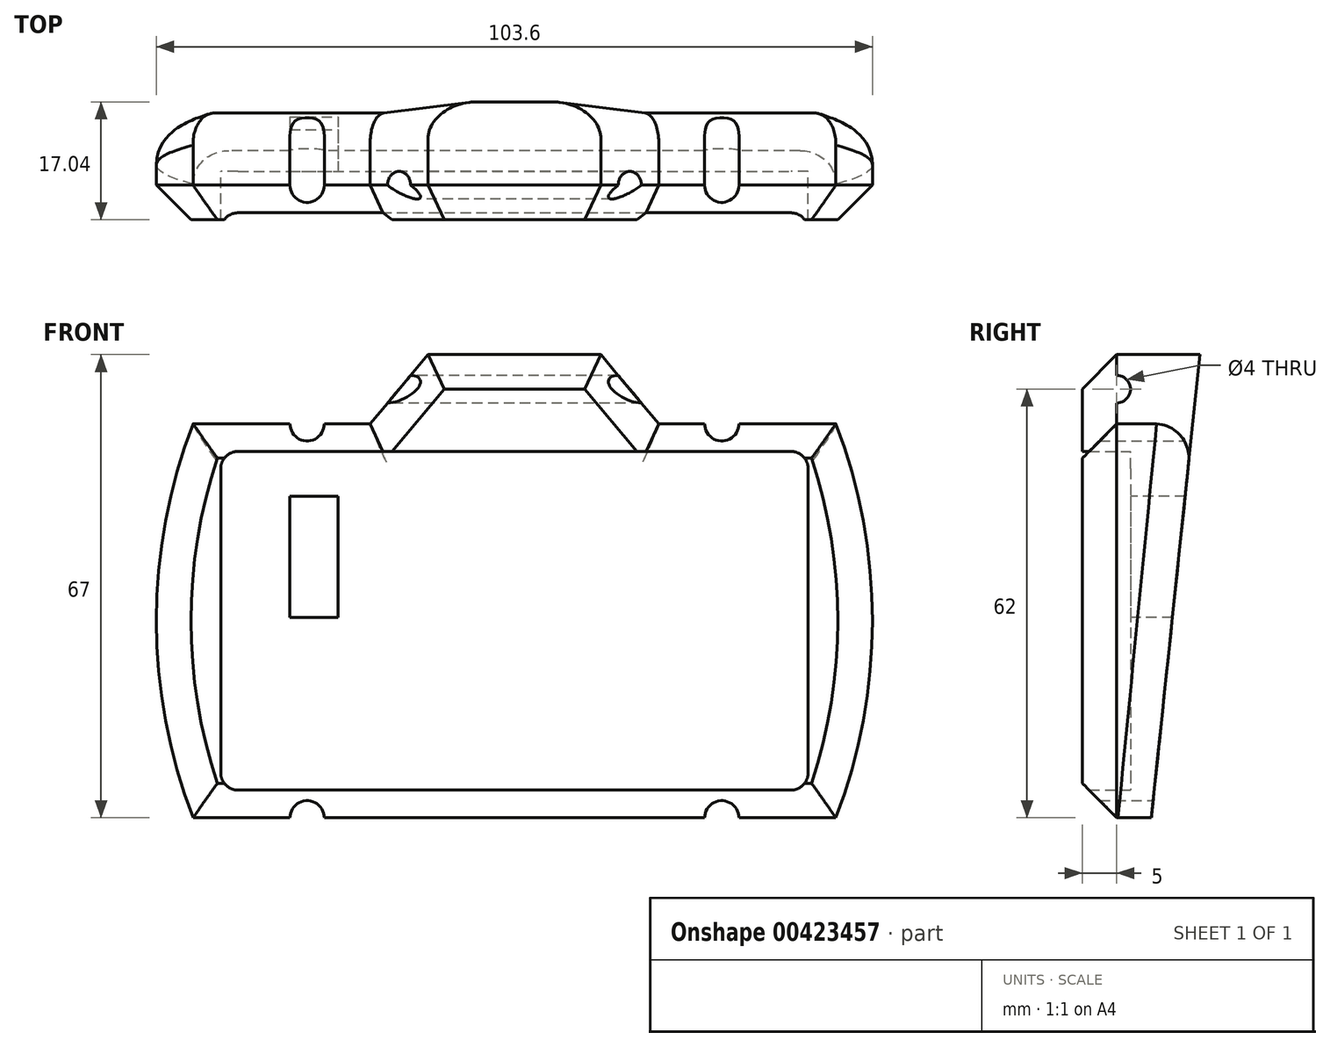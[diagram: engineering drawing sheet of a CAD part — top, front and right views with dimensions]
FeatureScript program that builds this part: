
annotation { "Feature Type Name" : "Feature", "Feature Type Description" : "" }
export const myFeature = defineFeature(function(context is Context, id is Id, definition is map)
    precondition{}
    {
        {
            var Q0;
            Q0=qCreatedBy(makeId("Front.planeOp"),FACE);
            var sketch = newSketch(context, id + "F0", { "sketchPlane" : qUnion([Q0])});
            skLineSegment(sketch, "E0.bottom", {"start": v(86.5, 4) * mm, "end": v(6.5, 4) * mm});
            skLineSegment(sketch, "E0.top", {"start": v(86.5, 53) * mm, "end": v(6.5, 53) * mm});
            skLineSegment(sketch, "E0.left", {"start": v(89, 6.5) * mm, "end": v(89, 50.5) * mm});
            skLineSegment(sketch, "E0.right", {"start": v(4, 6.5) * mm, "end": v(4, 50.5) * mm});
            skPoint(sketch, "E1.visualSharp", {"position": v(89, 4) * mm});
            skArc(sketch, "E1.filletArc", {"start": v(86.5, 4) * mm, "mid": v(88.27, 4.73) * mm, "end": v(89, 6.5) * mm});
            skPoint(sketch, "E2.visualSharp", {"position": v(89, 53) * mm});
            skArc(sketch, "E2.filletArc", {"start": v(89, 50.5) * mm, "mid": v(88.27, 52.27) * mm, "end": v(86.5, 53) * mm});
            skPoint(sketch, "E3.visualSharp", {"position": v(4, 53) * mm});
            skArc(sketch, "E3.filletArc", {"start": v(6.5, 53) * mm, "mid": v(4.73, 52.27) * mm, "end": v(4, 50.5) * mm});
            skPoint(sketch, "E4.visualSharp", {"position": v(4, 4) * mm});
            skArc(sketch, "E4.filletArc", {"start": v(4, 6.5) * mm, "mid": v(4.73, 4.73) * mm, "end": v(6.5, 4) * mm});
            skLineSegment(sketch, "E5.bottom", {"start": v(0, 57) * mm, "end": v(93, 57) * mm});
            skLineSegment(sketch, "E5.top", {"start": v(0, 0) * mm, "end": v(93, 0) * mm});
            skLineSegment(sketch, "E5.left", {"start": v(0, 57) * mm, "end": v(0, 0) * mm});
            skLineSegment(sketch, "E5.right", {"start": v(93, 57) * mm, "end": v(93, 0) * mm});
            skArc(sketch, "E6", {"start": v(0, 57) * mm, "mid": v(-5.3, 28.5) * mm, "end": v(0, 0) * mm});
            skArc(sketch, "E7", {"start": v(93, 0) * mm, "mid": v(98.3, 28.5) * mm, "end": v(93, 57) * mm});
            skPoint(sketch, "E8", {"position": v(-5.3, 28.5) * mm});
            skLineSegment(sketch, "E9", {"start": v(34, 67) * mm, "end": v(59, 67) * mm});
            skLineSegment(sketch, "E10", {"start": v(34, 67) * mm, "end": v(25.6, 57) * mm});
            skLineSegment(sketch, "E11", {"start": v(59, 67) * mm, "end": v(67.4, 57) * mm});
            skLineSegment(sketch, "E12", {"start": v(34, 67) * mm, "end": v(34, 57) * mm});
            skLineSegment(sketch, "E13", {"start": v(59, 67) * mm, "end": v(59, 57) * mm});
            skSolve(sketch);
        }
        {
            var Q0;
            Q0=makeQuery(id+"F0.imprint","IMPRINT",FACE,{"disambiguationData":[TD([[makeQuery(id+"F0.imprint","IMPRINT",EDGE,{"derivedFrom":sQuery(id+"F0.wireOp",EDGE,"E0.bottom")}),-1.0]])]});
            var Q1;
            Q1=makeQuery(id+"F0.imprint","IMPRINT",FACE,{"disambiguationData":[TD([[makeQuery(id+"F0.imprint","IMPRINT",EDGE,{"derivedFrom":sQuery(id+"F0.wireOp",EDGE,"E0.bottom")}),1.0]])]});
            var Q2;
            Q2=makeQuery(id+"F0.imprint","IMPRINT",FACE,{"disambiguationData":[TD([[makeQuery(id+"F0.imprint","IMPRINT",EDGE,{"derivedFrom":sQuery(id+"F0.wireOp",EDGE,"E5.left")}),-1.0]])]});
            var Q3;
            Q3=makeQuery(id+"F0.imprint","IMPRINT",FACE,{"disambiguationData":[TD([[makeQuery(id+"F0.imprint","IMPRINT",EDGE,{"derivedFrom":sQuery(id+"F0.wireOp",EDGE,"E5.right")}),1.0]])]});
            var Q4;
            {var subQ0=sQuery(id+"F0.wireOp",EDGE,"3fx2YpcI-U5EB-vFxf-iBCI-2TCYV5EJUoEd");Q4=makeQuery(id+"F0.imprint","IMPRINT",FACE,{"disambiguationData":[TD([[makeQuery(id+"F0.imprint","IMPRINT",EDGE,{"derivedFrom":subQ0}),-1.0]])]});}
            var Q5;
            {var subQ0=sQuery(id+"F0.wireOp",EDGE,"nPDYfrPs-5EqB-b0Kh-mRlZ-kWoabQpu5ybp");Q5=makeQuery(id+"F0.imprint","IMPRINT",FACE,{"disambiguationData":[TD([[makeQuery(id+"F0.imprint","IMPRINT",EDGE,{"derivedFrom":subQ0}),-1.0]])]});}
            var Q6;
            {var subQ0=sQuery(id+"F0.wireOp",EDGE,"nPDYfrPs-5EqB-b0Kh-mRlZ-kWoabQpu5ybp");Q6=makeQuery(id+"F0.imprint","IMPRINT",FACE,{"disambiguationData":[TD([[makeQuery(id+"F0.imprint","IMPRINT",EDGE,{"derivedFrom":subQ0}),1.0]])]});}
            var Q7;
            Q7=makeQuery(id+"F0.imprint","IMPRINT",FACE,{"disambiguationData":[TD([[makeQuery(id+"F0.imprint","IMPRINT",EDGE,{"derivedFrom":sQuery(id+"F0.wireOp",EDGE,"E9")}),-1.0]])]});
            var Q8;
            {var subQ0=sQuery(id+"F0.wireOp",EDGE,"E10");Q8=makeQuery(id+"F0.imprint","IMPRINT",FACE,{"disambiguationData":[TD([[makeQuery(id+"F0.imprint","IMPRINT",EDGE,{"derivedFrom":subQ0}),1.0]])]});}
            var Q9;
            {var subQ0=sQuery(id+"F0.wireOp",EDGE,"E11");Q9=makeQuery(id+"F0.imprint","IMPRINT",FACE,{"disambiguationData":[TD([[makeQuery(id+"F0.imprint","IMPRINT",EDGE,{"derivedFrom":subQ0}),-1.0]])]});}
            extrude(context, id + "F1", {"entities" : qUnion([Q0, Q1, Q2, Q3, Q4, Q5, Q6, Q7, Q8, Q9]), "depth" : 3 * mm, "offsetDistance" : 25 * mm});
        }
        {
            var Q0;
            Q0=makeQuery(id+"F0.imprint","IMPRINT",FACE,{"disambiguationData":[TD([[makeQuery(id+"F0.imprint","IMPRINT",EDGE,{"derivedFrom":sQuery(id+"F0.wireOp",EDGE,"E9")}),-1.0]])]});
            var Q1;
            {var subQ0=sQuery(id+"F0.wireOp",EDGE,"E10");Q1=makeQuery(id+"F0.imprint","IMPRINT",FACE,{"disambiguationData":[TD([[makeQuery(id+"F0.imprint","IMPRINT",EDGE,{"derivedFrom":subQ0}),1.0]])]});}
            var Q2;
            {var subQ0=sQuery(id+"F0.wireOp",EDGE,"E11");Q2=makeQuery(id+"F0.imprint","IMPRINT",FACE,{"disambiguationData":[TD([[makeQuery(id+"F0.imprint","IMPRINT",EDGE,{"derivedFrom":subQ0}),-1.0]])]});}
            var Q3;
            Q3=makeQuery(id+"F0.imprint","IMPRINT",FACE,{"disambiguationData":[TD([[makeQuery(id+"F0.imprint","IMPRINT",EDGE,{"derivedFrom":sQuery(id+"F0.wireOp",EDGE,"E0.bottom")}),1.0]])]});
            var Q4;
            Q4=makeQuery(id+"F0.imprint","IMPRINT",FACE,{"disambiguationData":[TD([[makeQuery(id+"F0.imprint","IMPRINT",EDGE,{"derivedFrom":sQuery(id+"F0.wireOp",EDGE,"E5.right")}),1.0]])]});
            var Q5;
            Q5=makeQuery(id+"F0.imprint","IMPRINT",FACE,{"disambiguationData":[TD([[makeQuery(id+"F0.imprint","IMPRINT",EDGE,{"derivedFrom":sQuery(id+"F0.wireOp",EDGE,"E5.left")}),-1.0]])]});
            extrude(context, id + "F2", {"entities" : qUnion([Q0, Q1, Q2, Q3, Q4, Q5]), "operationType" : NewBodyOperationType.ADD, "depth" : 10 * mm, "offsetDistance" : 25 * mm});
        }
        {
            var Q0;
            Q0=qCreatedBy(makeId("Right.planeOp"),FACE);
            var sketch = newSketch(context, id + "F3", { "sketchPlane" : qUnion([Q0])});
            skLineSegment(sketch, "E14.0", {"start": v(0, 0) * mm, "end": v(0, 57) * mm});
            skLineSegment(sketch, "E14.1", {"start": v(0, 67) * mm, "end": v(0, 57) * mm});
            skLineSegment(sketch, "E14.2", {"start": v(10, 67) * mm, "end": v(0, 67) * mm});
            skLineSegment(sketch, "E14.3", {"start": v(10, 67) * mm, "end": v(10, 57) * mm});
            skLineSegment(sketch, "E14.4", {"start": v(10, 0) * mm, "end": v(10, 57) * mm});
            skLineSegment(sketch, "E14.5", {"start": v(10, 0) * mm, "end": v(0, 0) * mm});
            skLineSegment(sketch, "E15", {"start": v(0, 0) * mm, "end": v(7.04, 67) * mm});
            skSolve(sketch);
        }
        {
            var Q0;
            Q0=makeQuery(id+"F1.opExtrude","CAP_FACE",FACE,{"disambiguationData":[OSD([sQuery(id+"F0.wireOp",EDGE,"E5.bottom"),sQuery(id+"F0.wireOp",EDGE,"E5.top"),sQuery(id+"F0.wireOp",EDGE,"E6"),sQuery(id+"F0.wireOp",EDGE,"E7"),sQuery(id+"F0.wireOp",EDGE,"E9"),sQuery(id+"F0.wireOp",EDGE,"E10"),sQuery(id+"F0.wireOp",EDGE,"E11")])],"isStart":true});
            extrude(context, id + "F4", {"entities" : qUnion([Q0]), "operationType" : NewBodyOperationType.ADD, "depth" : 10 * mm, "offsetDistance" : 25 * mm});
        }
        {
            var Q0;
            {var subQ0=sQuery(id+"F3.wireOp",EDGE,"E14.3");Q0=makeQuery(id+"F3.imprint","IMPRINT",FACE,{"disambiguationData":[TD([[makeQuery(id+"F3.imprint","IMPRINT",EDGE,{"derivedFrom":subQ0}),-1.0]])]});}
            extrude(context, id + "F5", {"entities" : qUnion([Q0]), "operationType" : NewBodyOperationType.REMOVE, "endBound" : BoundingType.SYMMETRIC, "depth" : 300 * mm, "offsetDistance" : 25 * mm});
        }
        {
            var Q0;
            Q0=makeQuery(id+"F2.opExtrude","SWEPT_FACE",FACE,{"disambiguationData":[OSD([sQuery(id+"F0.wireOp",EDGE,"E0.right")])]});
            var sketch = newSketch(context, id + "F6", { "sketchPlane" : qUnion([Q0])});
            skLineSegment(sketch, "E16.0.0", {"start": v(0, 67) * mm, "end": v(0, 57) * mm});
            skLineSegment(sketch, "E16.0.1", {"start": v(0, 57) * mm, "end": v(-10, 57) * mm});
            skLineSegment(sketch, "E16.0.2", {"start": v(-10, 57) * mm, "end": v(-10, 67) * mm});
            skLineSegment(sketch, "E16.0.3", {"start": v(-10, 67) * mm, "end": v(0, 67) * mm});
            skCircle(sketch, "E17", {"center": v(-5, 62) * mm, "radius": 2 * mm});
            skSolve(sketch);
        }
        {
            var Q0;
            Q0=makeQuery(id+"F6.imprint","IMPRINT",FACE,{"disambiguationData":[TD([[makeQuery(id+"F6.imprint","IMPRINT",EDGE,{"derivedFrom":sQuery(id+"F6.wireOp",EDGE,"E17")}),1.0]])]});
            extrude(context, id + "F7", {"entities" : qUnion([Q0]), "operationType" : NewBodyOperationType.REMOVE, "endBound" : BoundingType.THROUGH_ALL, "depth" : 25 * mm, "offsetDistance" : 25 * mm});
        }
        {
            var Q0;
            Q0=makeQuery(id+"F2.opExtrude","CAP_EDGE",EDGE,{"disambiguationData":[OSD([sQuery(id+"F0.wireOp",EDGE,"E6")])],"isStart":false});
            var Q1;
            {var subQ0=sQuery(id+"F0.wireOp",EDGE,"E5.bottom");Q1=makeQuery(id+"F2.opExtrude","CAP_EDGE",EDGE,{"disambiguationData":[OSD([subQ0]),TDD([makeQuery(id+"F0.imprint","IMPRINT",EDGE,{"disambiguationData":[TD([[makeQuery(id+"F0.imprint","INTERSECT",VERTEX,{"derivedFrom":[subQ0,sQuery(id+"F0.wireOp",EDGE,"E10")]}),1.0]])],"derivedFrom":subQ0})])],"isStart":false});}
            var Q2;
            Q2=makeQuery(id+"F2.opExtrude","CAP_EDGE",EDGE,{"disambiguationData":[OSD([sQuery(id+"F0.wireOp",EDGE,"E10")])],"isStart":false});
            var Q3;
            Q3=makeQuery(id+"F2.opExtrude","CAP_EDGE",EDGE,{"disambiguationData":[OSD([sQuery(id+"F0.wireOp",EDGE,"E9")])],"isStart":false});
            var Q4;
            Q4=makeQuery(id+"F2.opExtrude","CAP_EDGE",EDGE,{"disambiguationData":[OSD([sQuery(id+"F0.wireOp",EDGE,"E11")])],"isStart":false});
            var Q5;
            {var subQ0=sQuery(id+"F0.wireOp",EDGE,"E5.bottom");Q5=makeQuery(id+"F2.opExtrude","CAP_EDGE",EDGE,{"disambiguationData":[OSD([subQ0]),TDD([makeQuery(id+"F0.imprint","IMPRINT",EDGE,{"disambiguationData":[TD([[makeQuery(id+"F0.imprint","INTERSECT",VERTEX,{"derivedFrom":[subQ0,sQuery(id+"F0.wireOp",EDGE,"E11")]}),-1.0]])],"derivedFrom":subQ0})])],"isStart":false});}
            var Q6;
            Q6=makeQuery(id+"F2.opExtrude","CAP_EDGE",EDGE,{"disambiguationData":[OSD([sQuery(id+"F0.wireOp",EDGE,"E5.top")])],"isStart":false});
            var Q7;
            Q7=makeQuery(id+"F2.opExtrude","CAP_EDGE",EDGE,{"disambiguationData":[OSD([sQuery(id+"F0.wireOp",EDGE,"E7")])],"isStart":false});
            chamfer(context, id + "F8", {"entities" : qUnion([Q0, Q1, Q2, Q3, Q4, Q5, Q6, Q7]), "width" : 5 * mm, "tangentPropagation" : true});
        }
        {
            var Q0;
            Q0=makeQuery(id+"F1.opExtrude","CAP_FACE",FACE,{"disambiguationData":[OSD([sQuery(id+"F0.wireOp",EDGE,"E5.bottom"),sQuery(id+"F0.wireOp",EDGE,"E5.top"),sQuery(id+"F0.wireOp",EDGE,"E6"),sQuery(id+"F0.wireOp",EDGE,"E7"),sQuery(id+"F0.wireOp",EDGE,"E9"),sQuery(id+"F0.wireOp",EDGE,"E10"),sQuery(id+"F0.wireOp",EDGE,"E11")])],"isStart":false});
            var sketch = newSketch(context, id + "F9", { "sketchPlane" : qUnion([Q0])});
            skLineSegment(sketch, "E18.0", {"start": v(4, 6.5) * mm, "end": v(4, 50.5) * mm});
            skLineSegment(sketch, "E18.1", {"start": v(89, 6.5) * mm, "end": v(89, 50.5) * mm});
            skArc(sketch, "E19", {"start": v(14, 57) * mm, "mid": v(16.5, 54.5) * mm, "end": v(19, 57) * mm});
            skArc(sketch, "E20", {"start": v(19, 0) * mm, "mid": v(16.5, 2.5) * mm, "end": v(14, 0) * mm});
            skArc(sketch, "E21", {"start": v(74, 57) * mm, "mid": v(76.5, 54.5) * mm, "end": v(79, 57) * mm});
            skArc(sketch, "E22", {"start": v(79, 0) * mm, "mid": v(76.5, 2.5) * mm, "end": v(74, 0) * mm});
            skLineSegment(sketch, "E23", {"start": v(14, 57) * mm, "end": v(19, 57) * mm});
            skLineSegment(sketch, "E24", {"start": v(74, 57) * mm, "end": v(79, 57) * mm});
            skLineSegment(sketch, "E25", {"start": v(74, 0) * mm, "end": v(79, 0) * mm});
            skLineSegment(sketch, "E26", {"start": v(14, 0) * mm, "end": v(19, 0) * mm});
            skSolve(sketch);
        }
        {
            var Q0;
            {var subQ0=sQuery(id+"F9.wireOp",EDGE,"E19");Q0=makeQuery(id+"F9.imprint","IMPRINT",FACE,{"disambiguationData":[TD([[makeQuery(id+"F9.imprint","IMPRINT",EDGE,{"derivedFrom":subQ0}),1.0]])]});}
            var Q1;
            {var subQ0=sQuery(id+"F9.wireOp",EDGE,"E21");Q1=makeQuery(id+"F9.imprint","IMPRINT",FACE,{"disambiguationData":[TD([[makeQuery(id+"F9.imprint","IMPRINT",EDGE,{"derivedFrom":subQ0}),1.0]])]});}
            var Q2;
            {var subQ0=sQuery(id+"F9.wireOp",EDGE,"E22");Q2=makeQuery(id+"F9.imprint","IMPRINT",FACE,{"disambiguationData":[TD([[makeQuery(id+"F9.imprint","IMPRINT",EDGE,{"derivedFrom":subQ0}),1.0]])]});}
            var Q3;
            {var subQ0=sQuery(id+"F9.wireOp",EDGE,"E20");Q3=makeQuery(id+"F9.imprint","IMPRINT",FACE,{"disambiguationData":[TD([[makeQuery(id+"F9.imprint","IMPRINT",EDGE,{"derivedFrom":subQ0}),1.0]])]});}
            var Q4;
            Q4=sQuery(id+"F9.wireOp",EDGE,"E22");
            var Q5;
            Q5=sQuery(id+"F9.wireOp",EDGE,"E20");
            var Q6;
            Q6=sQuery(id+"F9.wireOp",EDGE,"E19");
            var Q7;
            Q7=sQuery(id+"F9.wireOp",EDGE,"E21");
            extrude(context, id + "F10", {"entities" : qUnion([Q0, Q1, Q2, Q3]), "operationType" : NewBodyOperationType.REMOVE, "surfaceEntities" : qUnion([Q4, Q5, Q6, Q7]), "endBound" : BoundingType.SYMMETRIC, "depth" : 25 * mm, "offsetDistance" : 25 * mm});
        }
        {
            var Q0;
            {var subQ0=sQuery(id+"F0.wireOp",EDGE,"E7");Q0=makeQuery(id+"F5.boolean.opBoolean","INTERSECT",EDGE,{"derivedFrom":[makeQuery(id+"F4.boolean.opBoolean","MERGE",FACE,{"derivedFrom":[makeQuery(id+"F2.boolean.opBoolean","MERGE",FACE,{"derivedFrom":[makeQuery(id+"F1.opExtrude","SWEPT_FACE",FACE,{"disambiguationData":[OSD([subQ0])]}),makeQuery(id+"F2.opExtrude","SWEPT_FACE",FACE,{"disambiguationData":[OSD([subQ0])]})]}),makeQuery(id+"F4.opExtrude","SWEPT_FACE",FACE,{"disambiguationData":[OSD([subQ0])]})]}),makeQuery(id+"F5.opExtrude","SWEPT_FACE",FACE,{"disambiguationData":[OSD([sQuery(id+"F3.wireOp",EDGE,"E15")])]})]});}
            var Q1;
            {var subQ0=sQuery(id+"F0.wireOp",EDGE,"E5.bottom");var subQ1=makeQuery(id+"F0.imprint","IMPRINT",EDGE,{"disambiguationData":[TD([[makeQuery(id+"F0.imprint","INTERSECT",VERTEX,{"derivedFrom":[subQ0,sQuery(id+"F0.wireOp",EDGE,"E11")]}),-1.0]])],"derivedFrom":subQ0});Q1=makeQuery(id+"F5.boolean.opBoolean","INTERSECT",EDGE,{"derivedFrom":[makeQuery(id+"F4.boolean.opBoolean","MERGE",FACE,{"derivedFrom":[makeQuery(id+"F2.boolean.opBoolean","MERGE",FACE,{"derivedFrom":[makeQuery(id+"F1.opExtrude","SWEPT_FACE",FACE,{"disambiguationData":[OSD([subQ0]),TDD([subQ1])]}),makeQuery(id+"F2.opExtrude","SWEPT_FACE",FACE,{"disambiguationData":[OSD([subQ0]),TDD([subQ1])]})]}),makeQuery(id+"F4.opExtrude","SWEPT_FACE",FACE,{"disambiguationData":[OSD([subQ0]),TDD([makeQuery(id+"F1.opExtrude","CAP_EDGE",EDGE,{"disambiguationData":[OSD([subQ0]),TDD([subQ1])],"isStart":true})])]})]}),makeQuery(id+"F5.opExtrude","SWEPT_FACE",FACE,{"disambiguationData":[OSD([sQuery(id+"F3.wireOp",EDGE,"E15")])]})]});}
            var Q2;
            {var subQ0=sQuery(id+"F0.wireOp",EDGE,"E11");Q2=makeQuery(id+"F5.boolean.opBoolean","INTERSECT",EDGE,{"derivedFrom":[makeQuery(id+"F4.boolean.opBoolean","MERGE",FACE,{"derivedFrom":[makeQuery(id+"F2.boolean.opBoolean","MERGE",FACE,{"derivedFrom":[makeQuery(id+"F1.opExtrude","SWEPT_FACE",FACE,{"disambiguationData":[OSD([subQ0])]}),makeQuery(id+"F2.opExtrude","SWEPT_FACE",FACE,{"disambiguationData":[OSD([subQ0])]})]}),makeQuery(id+"F4.opExtrude","SWEPT_FACE",FACE,{"disambiguationData":[OSD([subQ0])]})]}),makeQuery(id+"F5.opExtrude","SWEPT_FACE",FACE,{"disambiguationData":[OSD([sQuery(id+"F3.wireOp",EDGE,"E15")])]})]});}
            var Q3;
            Q3=makeQuery(id+"F5.boolean.opBoolean","COPY",EDGE,{"derivedFrom":makeQuery(id+"F5.opExtrude","SWEPT_EDGE",EDGE,{"disambiguationData":[OSD([sQuery(id+"F3.wireOp",EDGE,"E14.2"),sQuery(id+"F3.wireOp",EDGE,"E15")])]})});
            var Q4;
            {var subQ0=sQuery(id+"F0.wireOp",EDGE,"E10");Q4=makeQuery(id+"F5.boolean.opBoolean","INTERSECT",EDGE,{"derivedFrom":[makeQuery(id+"F4.boolean.opBoolean","MERGE",FACE,{"derivedFrom":[makeQuery(id+"F2.boolean.opBoolean","MERGE",FACE,{"derivedFrom":[makeQuery(id+"F1.opExtrude","SWEPT_FACE",FACE,{"disambiguationData":[OSD([subQ0])]}),makeQuery(id+"F2.opExtrude","SWEPT_FACE",FACE,{"disambiguationData":[OSD([subQ0])]})]}),makeQuery(id+"F4.opExtrude","SWEPT_FACE",FACE,{"disambiguationData":[OSD([subQ0])]})]}),makeQuery(id+"F5.opExtrude","SWEPT_FACE",FACE,{"disambiguationData":[OSD([sQuery(id+"F3.wireOp",EDGE,"E15")])]})]});}
            var Q5;
            {var subQ0=sQuery(id+"F0.wireOp",EDGE,"E10");var subQ1=sQuery(id+"F0.wireOp",EDGE,"E5.bottom");var subQ2=makeQuery(id+"F0.imprint","IMPRINT",EDGE,{"disambiguationData":[TD([[makeQuery(id+"F0.imprint","INTERSECT",VERTEX,{"derivedFrom":[subQ1,subQ0]}),1.0]])],"derivedFrom":subQ1});var subQ3=makeQuery(id+"F4.opExtrude","SWEPT_FACE",FACE,{"disambiguationData":[OSD([subQ1]),TDD([makeQuery(id+"F1.opExtrude","CAP_EDGE",EDGE,{"disambiguationData":[OSD([subQ1]),TDD([subQ2])],"isStart":true})])]});var subQ4=makeQuery(id+"F2.opExtrude","SWEPT_FACE",FACE,{"disambiguationData":[OSD([subQ1]),TDD([subQ2])]});var subQ5=makeQuery(id+"F1.opExtrude","SWEPT_FACE",FACE,{"disambiguationData":[OSD([subQ1]),TDD([subQ2])]});var subQ6=makeQuery(id+"F5.opExtrude","SWEPT_FACE",FACE,{"disambiguationData":[OSD([sQuery(id+"F3.wireOp",EDGE,"E15")])]});Q5=makeQuery(id+"F10.boolean.opBoolean","SPLIT",EDGE,{"disambiguationData":[TD([makeQuery(id+"F1.opExtrude","SWEPT_FACE",FACE,{"disambiguationData":[OSD([subQ0])]})])],"derivedFrom":makeQuery(id+"F5.boolean.opBoolean","INTERSECT",EDGE,{"derivedFrom":[makeQuery(id+"F4.boolean.opBoolean","MERGE",FACE,{"derivedFrom":[makeQuery(id+"F2.boolean.opBoolean","MERGE",FACE,{"derivedFrom":[subQ5,subQ4]}),subQ3]}),subQ6]})});}
            var Q6;
            {var subQ0=sQuery(id+"F0.wireOp",EDGE,"E6");var subQ1=sQuery(id+"F0.wireOp",EDGE,"E5.bottom");var subQ2=makeQuery(id+"F0.imprint","IMPRINT",EDGE,{"disambiguationData":[TD([[makeQuery(id+"F0.imprint","INTERSECT",VERTEX,{"derivedFrom":[subQ1,sQuery(id+"F0.wireOp",EDGE,"E10")]}),1.0]])],"derivedFrom":subQ1});var subQ3=makeQuery(id+"F2.opExtrude","SWEPT_FACE",FACE,{"disambiguationData":[OSD([subQ1]),TDD([subQ2])]});var subQ4=makeQuery(id+"F1.opExtrude","SWEPT_FACE",FACE,{"disambiguationData":[OSD([subQ1]),TDD([subQ2])]});var subQ5=makeQuery(id+"F4.opExtrude","SWEPT_FACE",FACE,{"disambiguationData":[OSD([subQ1]),TDD([makeQuery(id+"F1.opExtrude","CAP_EDGE",EDGE,{"disambiguationData":[OSD([subQ1]),TDD([subQ2])],"isStart":true})])]});var subQ6=makeQuery(id+"F5.opExtrude","SWEPT_FACE",FACE,{"disambiguationData":[OSD([sQuery(id+"F3.wireOp",EDGE,"E15")])]});Q6=makeQuery(id+"F10.boolean.opBoolean","SPLIT",EDGE,{"disambiguationData":[TD([makeQuery(id+"F1.opExtrude","SWEPT_FACE",FACE,{"disambiguationData":[OSD([subQ0])]})])],"derivedFrom":makeQuery(id+"F5.boolean.opBoolean","INTERSECT",EDGE,{"derivedFrom":[makeQuery(id+"F4.boolean.opBoolean","MERGE",FACE,{"derivedFrom":[makeQuery(id+"F2.boolean.opBoolean","MERGE",FACE,{"derivedFrom":[subQ4,subQ3]}),subQ5]}),subQ6]})});}
            var Q7;
            {var subQ0=sQuery(id+"F0.wireOp",EDGE,"E6");Q7=makeQuery(id+"F5.boolean.opBoolean","INTERSECT",EDGE,{"derivedFrom":[makeQuery(id+"F4.boolean.opBoolean","MERGE",FACE,{"derivedFrom":[makeQuery(id+"F2.boolean.opBoolean","MERGE",FACE,{"derivedFrom":[makeQuery(id+"F1.opExtrude","SWEPT_FACE",FACE,{"disambiguationData":[OSD([subQ0])]}),makeQuery(id+"F2.opExtrude","SWEPT_FACE",FACE,{"disambiguationData":[OSD([subQ0])]})]}),makeQuery(id+"F4.opExtrude","SWEPT_FACE",FACE,{"disambiguationData":[OSD([subQ0])]})]}),makeQuery(id+"F5.opExtrude","SWEPT_FACE",FACE,{"disambiguationData":[OSD([sQuery(id+"F3.wireOp",EDGE,"E15")])]})]});}
            var Q8;
            {var subQ0=sQuery(id+"F0.wireOp",EDGE,"E5.top");var subQ1=sQuery(id+"F0.wireOp",EDGE,"E6");var subQ2=sQuery(id+"F3.wireOp",EDGE,"E15");Q8=makeQuery(id+"F10.boolean.opBoolean","SPLIT",EDGE,{"disambiguationData":[TD([makeQuery(id+"F1.opExtrude","SWEPT_FACE",FACE,{"disambiguationData":[OSD([subQ0])]}),makeQuery(id+"F1.opExtrude","SWEPT_FACE",FACE,{"disambiguationData":[OSD([subQ1])]}),makeQuery(id+"F2.opExtrude","SWEPT_FACE",FACE,{"disambiguationData":[OSD([subQ0])]}),makeQuery(id+"F2.opExtrude","SWEPT_FACE",FACE,{"disambiguationData":[OSD([subQ1])]}),makeQuery(id+"F4.opExtrude","SWEPT_FACE",FACE,{"disambiguationData":[OSD([subQ0])]}),makeQuery(id+"F4.opExtrude","SWEPT_FACE",FACE,{"disambiguationData":[OSD([subQ1])]}),makeQuery(id+"F5.boolean.opBoolean","COPY",FACE,{"derivedFrom":makeQuery(id+"F5.opExtrude","SWEPT_FACE",FACE,{"disambiguationData":[OSD([subQ2])]})}),makeQuery(id+"F10.opExtrude","SWEPT_FACE",FACE,{"disambiguationData":[OSD([sQuery(id+"F9.wireOp",EDGE,"E20")])]})])],"derivedFrom":makeQuery(id+"F5.boolean.opBoolean","COPY",EDGE,{"derivedFrom":makeQuery(id+"F5.opExtrude","SWEPT_EDGE",EDGE,{"disambiguationData":[OSD([sQuery(id+"F3.wireOp",EDGE,"E14.0"),sQuery(id+"F3.wireOp",EDGE,"E14.5"),subQ2])]})})});}
            var Q9;
            {var subQ0=sQuery(id+"F0.wireOp",EDGE,"E5.top");var subQ1=sQuery(id+"F3.wireOp",EDGE,"E15");Q9=makeQuery(id+"F10.boolean.opBoolean","SPLIT",EDGE,{"disambiguationData":[TD([makeQuery(id+"F1.opExtrude","SWEPT_FACE",FACE,{"disambiguationData":[OSD([subQ0])]}),makeQuery(id+"F2.opExtrude","SWEPT_FACE",FACE,{"disambiguationData":[OSD([subQ0])]}),makeQuery(id+"F4.opExtrude","SWEPT_FACE",FACE,{"disambiguationData":[OSD([subQ0])]}),makeQuery(id+"F5.boolean.opBoolean","COPY",FACE,{"derivedFrom":makeQuery(id+"F5.opExtrude","SWEPT_FACE",FACE,{"disambiguationData":[OSD([subQ1])]})}),makeQuery(id+"F10.opExtrude","SWEPT_FACE",FACE,{"disambiguationData":[OSD([sQuery(id+"F9.wireOp",EDGE,"E20")])]}),makeQuery(id+"F10.opExtrude","SWEPT_FACE",FACE,{"disambiguationData":[OSD([sQuery(id+"F9.wireOp",EDGE,"E22")])]})])],"derivedFrom":makeQuery(id+"F5.boolean.opBoolean","COPY",EDGE,{"derivedFrom":makeQuery(id+"F5.opExtrude","SWEPT_EDGE",EDGE,{"disambiguationData":[OSD([sQuery(id+"F3.wireOp",EDGE,"E14.0"),sQuery(id+"F3.wireOp",EDGE,"E14.5"),subQ1])]})})});}
            var Q10;
            {var subQ0=sQuery(id+"F0.wireOp",EDGE,"E7");var subQ1=sQuery(id+"F0.wireOp",EDGE,"E5.top");var subQ2=sQuery(id+"F3.wireOp",EDGE,"E15");Q10=makeQuery(id+"F10.boolean.opBoolean","SPLIT",EDGE,{"disambiguationData":[TD([makeQuery(id+"F1.opExtrude","SWEPT_FACE",FACE,{"disambiguationData":[OSD([subQ1])]}),makeQuery(id+"F1.opExtrude","SWEPT_FACE",FACE,{"disambiguationData":[OSD([subQ0])]}),makeQuery(id+"F2.opExtrude","SWEPT_FACE",FACE,{"disambiguationData":[OSD([subQ1])]}),makeQuery(id+"F2.opExtrude","SWEPT_FACE",FACE,{"disambiguationData":[OSD([subQ0])]}),makeQuery(id+"F4.opExtrude","SWEPT_FACE",FACE,{"disambiguationData":[OSD([subQ1])]}),makeQuery(id+"F4.opExtrude","SWEPT_FACE",FACE,{"disambiguationData":[OSD([subQ0])]}),makeQuery(id+"F5.boolean.opBoolean","COPY",FACE,{"derivedFrom":makeQuery(id+"F5.opExtrude","SWEPT_FACE",FACE,{"disambiguationData":[OSD([subQ2])]})}),makeQuery(id+"F10.opExtrude","SWEPT_FACE",FACE,{"disambiguationData":[OSD([sQuery(id+"F9.wireOp",EDGE,"E22")])]})])],"derivedFrom":makeQuery(id+"F5.boolean.opBoolean","COPY",EDGE,{"derivedFrom":makeQuery(id+"F5.opExtrude","SWEPT_EDGE",EDGE,{"disambiguationData":[OSD([sQuery(id+"F3.wireOp",EDGE,"E14.0"),sQuery(id+"F3.wireOp",EDGE,"E14.5"),subQ2])]})})});}
            fillet(context, id + "F11", {"entities" : qUnion([Q0, Q1, Q2, Q3, Q4, Q5, Q6, Q7, Q8, Q9, Q10]), "radius" : 5 * mm, "tangentPropagation" : true, "allowEdgeOverflow" : false});
        }
        {
            var Q0;
            Q0=makeQuery(id+"F1.opExtrude","CAP_FACE",FACE,{"disambiguationData":[OSD([sQuery(id+"F0.wireOp",EDGE,"E5.bottom"),sQuery(id+"F0.wireOp",EDGE,"E5.top"),sQuery(id+"F0.wireOp",EDGE,"E6"),sQuery(id+"F0.wireOp",EDGE,"E7"),sQuery(id+"F0.wireOp",EDGE,"E9"),sQuery(id+"F0.wireOp",EDGE,"E10"),sQuery(id+"F0.wireOp",EDGE,"E11")])],"isStart":false});
            var sketch = newSketch(context, id + "F12", { "sketchPlane" : qUnion([Q0])});
            skLineSegment(sketch, "E27.bottom", {"start": v(14, 46.5) * mm, "end": v(21, 46.5) * mm});
            skLineSegment(sketch, "E27.top", {"start": v(14, 29) * mm, "end": v(21, 29) * mm});
            skLineSegment(sketch, "E27.left", {"start": v(14, 46.5) * mm, "end": v(14, 29) * mm});
            skLineSegment(sketch, "E27.right", {"start": v(21, 46.5) * mm, "end": v(21, 29) * mm});
            skSolve(sketch);
        }
        {
            var Q0;
            Q0=makeQuery(id+"F12.imprint","IMPRINT",FACE,{"disambiguationData":[TD([[makeQuery(id+"F12.imprint","IMPRINT",EDGE,{"derivedFrom":sQuery(id+"F12.wireOp",EDGE,"E27.bottom")}),-1.0]])]});
            extrude(context, id + "F13", {"entities" : qUnion([Q0]), "operationType" : NewBodyOperationType.REMOVE, "oppositeDirection" : true, "depth" : 25 * mm, "offsetDistance" : 25 * mm});
        }
    });
